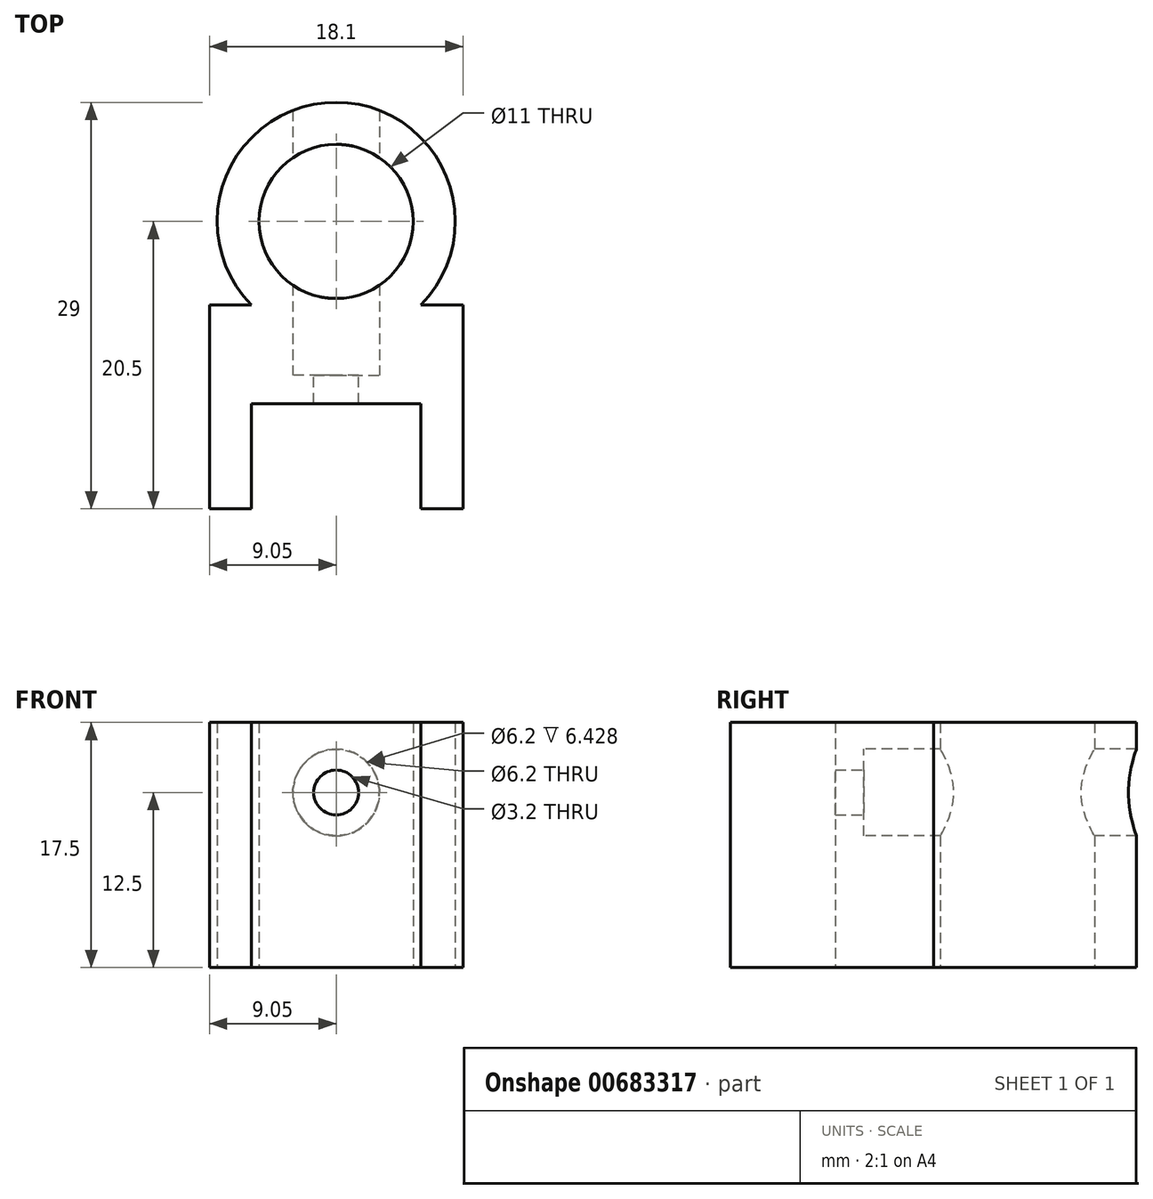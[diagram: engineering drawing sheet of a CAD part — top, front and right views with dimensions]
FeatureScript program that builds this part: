
annotation { "Feature Type Name" : "Feature", "Feature Type Description" : "" }
export const myFeature = defineFeature(function(context is Context, id is Id, definition is map)
    precondition{}
    {
        {
            var Q0;
            Q0=qCreatedBy(makeId("Top.planeOp"),FACE);
            var sketch = newSketch(context, id + "F0", { "sketchPlane" : qUnion([Q0])});
            skCircle(sketch, "E0", {"center": v(0, 0) * mm, "radius": 5.5 * mm});
            skCircle(sketch, "E1", {"center": v(0, 0) * mm, "radius": 8.5 * mm});
            skLineSegment(sketch, "E2.bottom", {"start": v(6.05, -13) * mm, "end": v(-6.05, -13) * mm});
            skLineSegment(sketch, "E2.top", {"start": v(6.05, 13) * mm, "end": v(-6.05, 13) * mm});
            skLineSegment(sketch, "E2.left", {"start": v(6.05, -13) * mm, "end": v(6.05, 13) * mm});
            skLineSegment(sketch, "E2.right", {"start": v(-6.05, -13) * mm, "end": v(-6.05, 13) * mm});
            skLineSegment(sketch, "E3", {"start": v(6.05, -13) * mm, "end": v(6.05, -20.5) * mm});
            skLineSegment(sketch, "E4.bottom", {"start": v(6.05, -20.5) * mm, "end": v(-6.05, -20.5) * mm});
            skLineSegment(sketch, "E4.left", {"start": v(6.05, -20.5) * mm, "end": v(6.05, -13) * mm});
            skLineSegment(sketch, "E4.right", {"start": v(-6.05, -20.5) * mm, "end": v(-6.05, -13) * mm});
            skLineSegment(sketch, "E5.bottom", {"start": v(-6.05, -20.5) * mm, "end": v(-9.05, -20.5) * mm});
            skLineSegment(sketch, "E5.top", {"start": v(-6.05, 13) * mm, "end": v(-9.05, 13) * mm});
            skLineSegment(sketch, "E5.left", {"start": v(-6.05, -20.5) * mm, "end": v(-6.05, 13) * mm});
            skLineSegment(sketch, "E5.right", {"start": v(-9.05, -20.5) * mm, "end": v(-9.05, 13) * mm});
            skLineSegment(sketch, "E6", {"start": v(0, 0) * mm, "end": v(0, -8.5) * mm});
            skLineSegment(sketch, "E7", {"start": v(0, -8.5) * mm, "end": v(0, -13) * mm});
            skLineSegment(sketch, "E8.bottom", {"start": v(6.05, -20.5) * mm, "end": v(9.05, -20.5) * mm});
            skLineSegment(sketch, "E8.top", {"start": v(6.05, 13) * mm, "end": v(9.05, 13) * mm});
            skLineSegment(sketch, "E8.left", {"start": v(6.05, -20.5) * mm, "end": v(6.05, 13) * mm});
            skLineSegment(sketch, "E8.right", {"start": v(9.05, -20.5) * mm, "end": v(9.05, 13) * mm});
            skLineSegment(sketch, "E9", {"start": v(6.05, -5.97) * mm, "end": v(9.05, -5.97) * mm});
            skLineSegment(sketch, "E10", {"start": v(-6.05, -5.97) * mm, "end": v(-9.05, -5.97) * mm});
            skLineSegment(sketch, "E11", {"start": v(-6.05, -5.97) * mm, "end": v(6.05, -5.97) * mm});
            skSolve(sketch);
        }
        {
            var Q0;
            {var subQ1=sQuery(id+"F0.wireOp",EDGE,"E5.bottom");Q0=makeQuery(id+"F0.imprint","IMPRINT",FACE,{"disambiguationData":[TD([[makeQuery(id+"F0.imprint","IMPRINT",EDGE,{"derivedFrom":subQ1}),-1.0]])]});}
            var Q1;
            {var subQ0=sQuery(id+"F0.wireOp",EDGE,"E7");Q1=makeQuery(id+"F0.imprint","IMPRINT",FACE,{"disambiguationData":[TD([[makeQuery(id+"F0.imprint","IMPRINT",EDGE,{"derivedFrom":subQ0}),-1.0]])]});}
            var Q2;
            {var subQ0=sQuery(id+"F0.wireOp",EDGE,"E7");Q2=makeQuery(id+"F0.imprint","IMPRINT",FACE,{"disambiguationData":[TD([[makeQuery(id+"F0.imprint","IMPRINT",EDGE,{"derivedFrom":subQ0}),1.0]])]});}
            var Q3;
            {var subQ1=sQuery(id+"F0.wireOp",EDGE,"E8.bottom");Q3=makeQuery(id+"F0.imprint","IMPRINT",FACE,{"disambiguationData":[TD([[makeQuery(id+"F0.imprint","IMPRINT",EDGE,{"derivedFrom":subQ1}),1.0]])]});}
            extrude(context, id + "F1", {"entities" : qUnion([Q0, Q1, Q2, Q3]), "depth" : 17.5 * mm, "offsetDistance" : 25 * mm});
        }
        {
            var Q0;
            Q0=makeQuery(id+"F0.imprint","IMPRINT",FACE,{"disambiguationData":[TD([[makeQuery(id+"F0.imprint","IMPRINT",EDGE,{"derivedFrom":sQuery(id+"F0.wireOp",EDGE,"E0")}),-1.0]])]});
            var Q1;
            {var subQ0=sQuery(id+"F0.wireOp",EDGE,"E8.left");var subQ1=sQuery(id+"F0.wireOp",EDGE,"E1");var subQ3=makeQuery(id+"F0.imprint","INTERSECT",VERTEX,{"derivedFrom":[subQ1,subQ0]});Q1=makeQuery(id+"F0.imprint","IMPRINT",FACE,{"disambiguationData":[TD([[makeQuery(id+"F0.imprint","IMPRINT",EDGE,{"disambiguationData":[TD([[subQ3,1.0]])],"derivedFrom":subQ1}),1.0]])]});}
            var Q2;
            {var subQ0=sQuery(id+"F0.wireOp",EDGE,"E5.left");var subQ1=sQuery(id+"F0.wireOp",EDGE,"E1");var subQ3=makeQuery(id+"F0.imprint","INTERSECT",VERTEX,{"derivedFrom":[subQ1,subQ0]});Q2=makeQuery(id+"F0.imprint","IMPRINT",FACE,{"disambiguationData":[TD([[makeQuery(id+"F0.imprint","IMPRINT",EDGE,{"disambiguationData":[TD([[subQ3,-1.0]])],"derivedFrom":subQ1}),1.0]])]});}
            var Q3;
            {var subQ0=sQuery(id+"F0.wireOp",EDGE,"E11");var subQ8=sQuery(id+"F0.wireOp",EDGE,"E0");var subQ10=makeQuery(id+"F0.imprint","INTERSECT",VERTEX,{"disambiguationData":[OD(0.0)],"derivedFrom":[subQ8,subQ0]});Q3=makeQuery(id+"F0.imprint","IMPRINT",FACE,{"disambiguationData":[TD([[makeQuery(id+"F0.imprint","IMPRINT",EDGE,{"disambiguationData":[TD([[subQ10,1.0]])],"derivedFrom":subQ8}),-1.0]])]});}
            var Q4;
            {var subQ0=sQuery(id+"F0.wireOp",EDGE,"E6");var subQ3=sQuery(id+"F0.wireOp",EDGE,"E11");var subQ5=makeQuery(id+"F0.imprint","INTERSECT",VERTEX,{"derivedFrom":[subQ0,subQ3]});Q4=makeQuery(id+"F0.imprint","IMPRINT",FACE,{"disambiguationData":[TD([[makeQuery(id+"F0.imprint","IMPRINT",EDGE,{"disambiguationData":[TD([[subQ5,-1.0]])],"derivedFrom":subQ0}),-1.0]])]});}
            var Q5;
            {var subQ0=sQuery(id+"F0.wireOp",EDGE,"E6");var subQ3=sQuery(id+"F0.wireOp",EDGE,"E11");var subQ5=makeQuery(id+"F0.imprint","INTERSECT",VERTEX,{"derivedFrom":[subQ0,subQ3]});Q5=makeQuery(id+"F0.imprint","IMPRINT",FACE,{"disambiguationData":[TD([[makeQuery(id+"F0.imprint","IMPRINT",EDGE,{"disambiguationData":[TD([[subQ5,-1.0]])],"derivedFrom":subQ0}),1.0]])]});}
            var Q6;
            {var subQ0=sQuery(id+"F0.wireOp",EDGE,"E8.right");var subQ1=sQuery(id+"F0.wireOp",EDGE,"E1");var subQ2=makeQuery(id+"F0.imprint","INTERSECT",VERTEX,{"disambiguationData":[OD(0.0)],"derivedFrom":[subQ1,subQ0]});Q6=makeQuery(id+"F0.imprint","IMPRINT",FACE,{"disambiguationData":[TD([[makeQuery(id+"F0.imprint","IMPRINT",EDGE,{"disambiguationData":[TD([[subQ2,1.0]])],"derivedFrom":subQ1}),1.0]])]});}
            var Q7;
            {var subQ0=sQuery(id+"F0.wireOp",EDGE,"E5.right");var subQ1=sQuery(id+"F0.wireOp",EDGE,"E1");var subQ2=makeQuery(id+"F0.imprint","INTERSECT",VERTEX,{"disambiguationData":[OD(0.0)],"derivedFrom":[subQ1,subQ0]});Q7=makeQuery(id+"F0.imprint","IMPRINT",FACE,{"disambiguationData":[TD([[makeQuery(id+"F0.imprint","IMPRINT",EDGE,{"disambiguationData":[TD([[subQ2,-1.0]])],"derivedFrom":subQ1}),1.0]])]});}
            extrude(context, id + "F2", {"entities" : qUnion([Q0, Q1, Q2, Q3, Q4, Q5, Q6, Q7]), "operationType" : NewBodyOperationType.ADD, "depth" : 9 * mm, "offsetDistance" : 25 * mm});
        }
        {
            var Q0;
            {var subQ0=sQuery(id+"F0.wireOp",EDGE,"E10");var subQ1=sQuery(id+"F0.wireOp",EDGE,"E1");Q0=makeQuery(id+"F2.boolean.opBoolean","SPLIT",EDGE,{"disambiguationData":[topologyDisambiguationEdgeConnected([makeQuery(id+"F2.opExtrude","SWEPT_FACE",FACE,{"disambiguationData":[OSD([subQ1])]})])],"derivedFrom":makeQuery(id+"F1.opExtrude","SWEPT_EDGE",EDGE,{"disambiguationData":[OSD([subQ1,sQuery(id+"F0.wireOp",EDGE,"E5.left"),subQ0,sQuery(id+"F0.wireOp",EDGE,"E11")])]})});}
            var Q1;
            {var subQ0=sQuery(id+"F0.wireOp",EDGE,"E9");var subQ1=sQuery(id+"F0.wireOp",EDGE,"E1");Q1=makeQuery(id+"F2.boolean.opBoolean","SPLIT",EDGE,{"disambiguationData":[topologyDisambiguationEdgeConnected([makeQuery(id+"F2.opExtrude","SWEPT_FACE",FACE,{"disambiguationData":[OSD([subQ1])]})])],"derivedFrom":makeQuery(id+"F1.opExtrude","SWEPT_EDGE",EDGE,{"disambiguationData":[OSD([subQ1,sQuery(id+"F0.wireOp",EDGE,"E8.left"),subQ0,sQuery(id+"F0.wireOp",EDGE,"E11")])]})});}
            fillet(context, id + "F3", {"entities" : qUnion([Q0, Q1]), "radius" : 20 * mm, "tangentPropagation" : true, "allowEdgeOverflow" : false});
        }
        {
            var Q0;
            Q0=makeQuery(id+"F1.opExtrude","SWEPT_FACE",FACE,{"disambiguationData":[OSD([sQuery(id+"F0.wireOp",EDGE,"E10"),sQuery(id+"F0.wireOp",EDGE,"E11")])]});
            var sketch = newSketch(context, id + "F4", { "sketchPlane" : qUnion([Q0])});
            skLineSegment(sketch, "E12", {"start": v(9.05, 17.5) * mm, "end": v(0, 17.5) * mm});
            skLineSegment(sketch, "E13", {"start": v(0, 17.5) * mm, "end": v(0, 12.5) * mm});
            skCircle(sketch, "E14", {"center": v(0, 12.5) * mm, "radius": 1.6 * mm});
            skCircle(sketch, "E15", {"center": v(0, 12.5) * mm, "radius": 3.1 * mm});
            skSolve(sketch);
        }
        {
            var Q0;
            Q0=makeQuery(id+"F2.opExtrude","CAP_FACE",FACE,{"disambiguationData":[OSD([sQuery(id+"F0.wireOp",EDGE,"E0"),sQuery(id+"F0.wireOp",EDGE,"E1")])],"isStart":false});
            var Q1;
            Q1=makeQuery(id+"F1.opExtrude","CAP_FACE",FACE,{"disambiguationData":[OSD([sQuery(id+"F0.wireOp",EDGE,"E1"),sQuery(id+"F0.wireOp",EDGE,"E2.bottom"),sQuery(id+"F0.wireOp",EDGE,"E5.bottom"),sQuery(id+"F0.wireOp",EDGE,"E5.left"),sQuery(id+"F0.wireOp",EDGE,"E5.right"),sQuery(id+"F0.wireOp",EDGE,"E8.bottom"),sQuery(id+"F0.wireOp",EDGE,"E8.left"),sQuery(id+"F0.wireOp",EDGE,"E8.right"),sQuery(id+"F0.wireOp",EDGE,"E9"),sQuery(id+"F0.wireOp",EDGE,"E10")])],"isStart":false});
            extrude(context, id + "F5", {"entities" : qUnion([Q0]), "operationType" : NewBodyOperationType.ADD, "endBound" : BoundingType.UP_TO_SURFACE, "depth" : 25 * mm, "endBoundEntityFace" : qUnion([Q1]), "offsetDistance" : 25 * mm});
        }
        {
            var Q0;
            Q0=makeQuery(id+"F4.imprint","IMPRINT",FACE,{"disambiguationData":[TD([[makeQuery(id+"F4.imprint","IMPRINT",EDGE,{"derivedFrom":sQuery(id+"F4.wireOp",EDGE,"E14")}),-1.0]])]});
            var Q1;
            Q1=makeQuery(id+"F4.imprint","IMPRINT",FACE,{"disambiguationData":[TD([[makeQuery(id+"F4.imprint","IMPRINT",EDGE,{"derivedFrom":sQuery(id+"F4.wireOp",EDGE,"E14")}),1.0]])]});
            extrude(context, id + "F6", {"entities" : qUnion([Q0, Q1]), "operationType" : NewBodyOperationType.REMOVE, "depth" : 25 * mm, "offsetDistance" : 25 * mm});
        }
        {
            var Q0;
            Q0 = qSketchRegion(id + "F4", true);
            extrude(context, id + "F7", {"entities" : qUnion([Q0]), "operationType" : NewBodyOperationType.REMOVE, "oppositeDirection" : true, "depth" : 5 * mm, "offsetDistance" : 25 * mm});
        }
        {
            var Q0;
            Q0=makeQuery(id+"F4.imprint","IMPRINT",FACE,{"disambiguationData":[TD([[makeQuery(id+"F4.imprint","IMPRINT",EDGE,{"derivedFrom":sQuery(id+"F4.wireOp",EDGE,"E14")}),1.0]])]});
            extrude(context, id + "F8", {"entities" : qUnion([Q0]), "operationType" : NewBodyOperationType.REMOVE, "oppositeDirection" : true, "depth" : 25 * mm, "offsetDistance" : 25 * mm});
        }
    });
